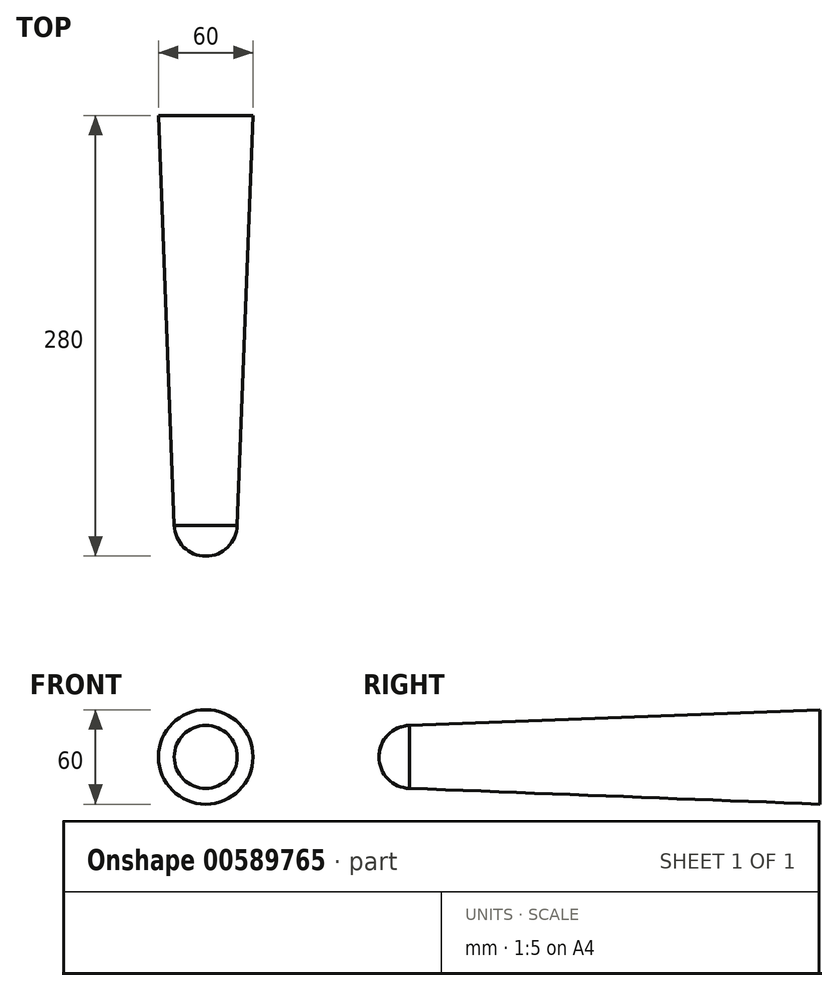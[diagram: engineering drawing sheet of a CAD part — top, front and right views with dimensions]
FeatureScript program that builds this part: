
annotation { "Feature Type Name" : "Feature", "Feature Type Description" : "" }
export const myFeature = defineFeature(function(context is Context, id is Id, definition is map)
    precondition{}
    {
        {
            var Q0;
            Q0=qCreatedBy(makeId("Right.planeOp"),FACE);
            var sketch = newSketch(context, id + "F0", { "sketchPlane" : qUnion([Q0])});
            skLineSegment(sketch, "E0", {"start": v(-142.35, 0) * mm, "end": v(137.65, 0) * mm});
            skArc(sketch, "E1", {"start": v(-142.35, 0) * mm, "mid": v(-136.67, 13.97) * mm, "end": v(-122.85, 20) * mm});
            skLineSegment(sketch, "E2", {"start": v(137.65, 0) * mm, "end": v(137.65, 30) * mm});
            skLineSegment(sketch, "E3", {"start": v(-122.85, 20) * mm, "end": v(137.65, 30) * mm});
            skSolve(sketch);
        }
        {
            var Q0;
            Q0=makeQuery(id+"F0.imprint","IMPRINT",FACE,{"disambiguationData":[TD([[makeQuery(id+"F0.imprint","IMPRINT",EDGE,{"derivedFrom":sQuery(id+"F0.wireOp",EDGE,"E0")}),1.0]])]});
            var Q1;
            Q1=sQuery(id+"F0.wireOp",EDGE,"E0");
            revolve(context, id + "F1", {"entities" : qUnion([Q0]), "axis" : qUnion([Q1]), "revolveType" : RevolveType.FULL});
        }
    });
